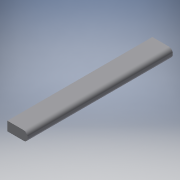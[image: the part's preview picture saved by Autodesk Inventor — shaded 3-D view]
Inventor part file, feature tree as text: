
AUTODESK INVENTOR PART (.ipt)
format: ipt  version: 2018 (Build 220112000, 112)  size: 112,640 bytes
history: native  units: mm
features: extrude x2, fillet x2, sketch x2
ambient origin geometry x8: Origin, YZ Plane, XZ Plane, XY Plane, X Axis, Y Axis, Z Axis, Center Point
bodies: Solid1 (feature_tree)
feature tree (6):
  extrude  "Extrusion1"  Depth=9.652mm
  fillet  "Fillet1"  Radius=76.2mm
  extrude  "Extrusion2"  Depth=1.0mm TaperAngle=0.0deg
  fillet  "Fillet2"  Radius=1.0mm
  sketch  "Sketch1"  dims[d0=4.826mm d1=9.652mm d2=76.2mm d3=0.0mm]
  sketch  "Sketch2"  dims[d4=2.0mm d5=1.0mm d6=0.0mm d7=1.0mm]
